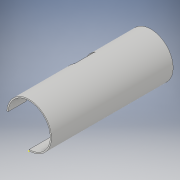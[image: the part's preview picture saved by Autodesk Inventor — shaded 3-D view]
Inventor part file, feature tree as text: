
AUTODESK INVENTOR PART (.ipt)
format: ipt  version: 2017 (Build 210142000, 142)  size: 181,760 bytes
history: native  units: in
note: dims shown in document units (in); Inventor stores cm internally (conversion verified against a paired STEP export)
features: sketch x11, extrude x4, plane x3, hole x1, mirror x1, other x1
ambient origin geometry x8: Origin, YZ Plane, XZ Plane, XY Plane, X Axis, Y Axis, Z Axis, Center Point
bodies: Solid1 (feature_tree)
feature tree (21):
  sketch  "Sketch1"  dims[d16=2.1654in d17=2.0472in]
  extrude  "Extrusion1"  Depth=2.0472in
  sketch  "Sketch3"  dims[d22=11.811in d23=0.0in d25=0.0481in]
  sketch  "Sketch4"  dims[d26=5.9055in d27=2.2441in]
  sketch  "Sketch5"  dims[d28=1.3386in d29=0.2644in]
  plane  "Work Plane1"
  hole  "Hole1"  [1 undecoded]
  extrude  "Extrusion2"  Depth=11.811in
  sketch  "Sketch8"  dims[d38=1.9685in]
  sketch  "Sketch9"  dims[d39=0.5906in]
  plane  "Work Plane2"
  extrude  "Extrusion3"  Depth=2.2441in
  extrude  "Extrusion4"  Depth=0.2644in
  plane  "Work Plane3"
  mirror  "Mirror1"
  sketch  "Sketch2"  dims[d18=0.0in d20=2.8346in]
  other  "Work Point1"
  sketch  "Sketch6"  dims[d30=0.2644in]
  sketch  "Sketch7"  dims[d31=0.1732in d32=0.2362in d33=0.1575in d34=0.0787in d35=90.0deg d36=0.315in d37=0.8108in]
  sketch  "Sketch10"  dims[d41=1.2992in]
  sketch  "Sketch12"  dims[d42=0.3937in d43=0.0in d44=0.3937in d45=0.0in d47=2.0472in d48=2.1654in d49=15.0deg d50=1.7717in d51=0.0in]
note: 1 required parameter value undecoded (feature->parameter linkage not recoverable at this tier; creation-order binding heuristic only, values carry confidence <= 0.55)
